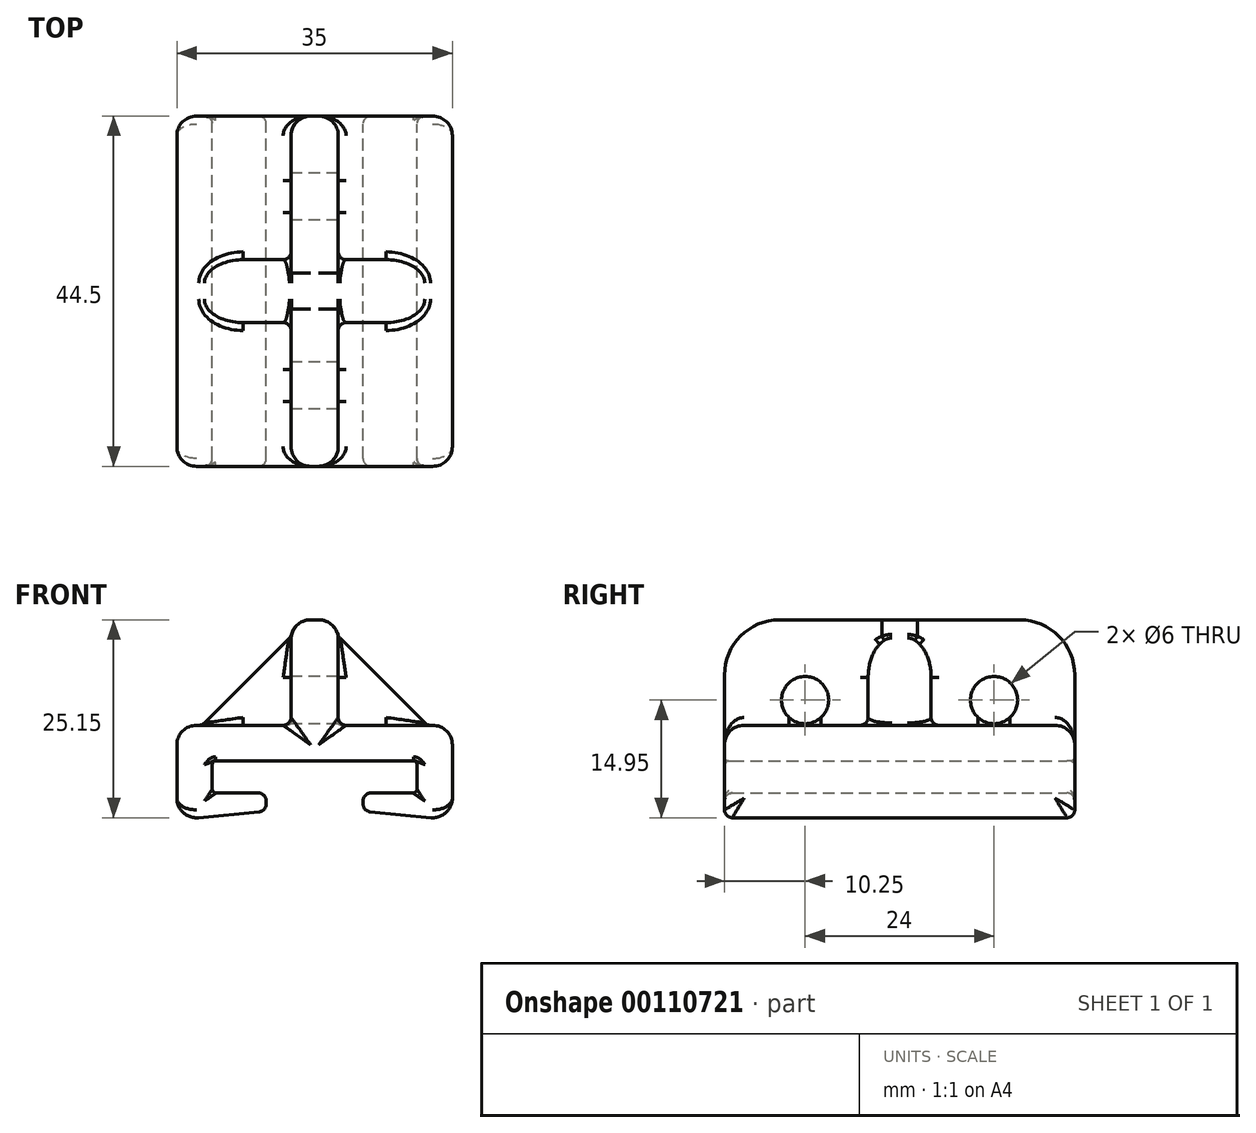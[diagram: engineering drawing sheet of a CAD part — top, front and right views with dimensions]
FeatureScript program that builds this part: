
annotation { "Feature Type Name" : "Feature", "Feature Type Description" : "" }
export const myFeature = defineFeature(function(context is Context, id is Id, definition is map)
    precondition{}
    {
        {
            var Q0;
            Q0=qCreatedBy(makeId("Front.planeOp"),FACE);
            var sketch = newSketch(context, id + "F0", { "sketchPlane" : qUnion([Q0])});
            skLineSegment(sketch, "E0", {"start": v(0, 0) * mm, "end": v(-13, 0) * mm});
            skLineSegment(sketch, "E1", {"start": v(-13, 0) * mm, "end": v(-13, -4.1) * mm});
            skLineSegment(sketch, "E2", {"start": v(-13, -4.1) * mm, "end": v(-6.15, -4.1) * mm});
            skLineSegment(sketch, "E3", {"start": v(-6.15, -4.1) * mm, "end": v(-6.15, -6.4) * mm});
            skLineSegment(sketch, "E4", {"start": v(-6.15, -6.4) * mm, "end": v(-17.5, -7.5) * mm});
            skLineSegment(sketch, "E5", {"start": v(-17.5, -7.5) * mm, "end": v(-17.5, 4.5) * mm});
            skLineSegment(sketch, "E6", {"start": v(-17.5, 4.5) * mm, "end": v(-3, 4.5) * mm});
            skLineSegment(sketch, "E7", {"start": v(-3, 4.5) * mm, "end": v(-3, 17.9) * mm});
            skLineSegment(sketch, "E8", {"start": v(-3, 17.9) * mm, "end": v(0, 17.9) * mm});
            skLineSegment(sketch, "E9.MirrorCS", {"start": v(6.15, -4.1) * mm, "end": v(6.15, -6.4) * mm});
            skLineSegment(sketch, "E10.MirrorCS", {"start": v(3, 17.9) * mm, "end": v(0, 17.9) * mm});
            skLineSegment(sketch, "E11.MirrorCS", {"start": v(13, -4.1) * mm, "end": v(6.15, -4.1) * mm});
            skLineSegment(sketch, "E12.MirrorCS", {"start": v(3, 4.5) * mm, "end": v(3, 17.9) * mm});
            skLineSegment(sketch, "E13.MirrorCS", {"start": v(17.5, 4.5) * mm, "end": v(3, 4.5) * mm});
            skLineSegment(sketch, "E14.MirrorCS", {"start": v(17.5, -7.5) * mm, "end": v(17.5, 4.5) * mm});
            skLineSegment(sketch, "E15.MirrorCS", {"start": v(6.15, -6.4) * mm, "end": v(17.5, -7.5) * mm});
            skLineSegment(sketch, "E16.MirrorCS", {"start": v(0, 0) * mm, "end": v(13, 0) * mm});
            skLineSegment(sketch, "E17.MirrorCS", {"start": v(13, 0) * mm, "end": v(13, -4.1) * mm});
            skSolve(sketch);
        }
        {
            var Q0;
            Q0=qSketchRegion(id+"F0",true);
            extrude(context, id + "F1", {"entities" : qUnion([Q0]), "depth" : 44.5 * mm, "symmetric" : true});
        }
        {
            var Q0;
            Q0=qCreatedBy(makeId("Front.planeOp"),FACE);
            var sketch = newSketch(context, id + "F2", { "sketchPlane" : qUnion([Q0])});
            skLineSegment(sketch, "E18.0", {"start": v(-3, 4.5) * mm, "end": v(-3, 15.8) * mm});
            skLineSegment(sketch, "E19.0", {"start": v(-14.3, 4.5) * mm, "end": v(-3, 4.5) * mm});
            skLineSegment(sketch, "E20", {"start": v(-14.3, 4.5) * mm, "end": v(-3, 15.8) * mm});
            skPoint(sketch, "E21.orphan", {"position": v(-3, 17.9) * mm});
            skPoint(sketch, "E22.orphan", {"position": v(-17.5, 4.5) * mm});
            skPoint(sketch, "E23.MirrorP", {"position": v(3, 17.9) * mm});
            skPoint(sketch, "E24.MirrorP", {"position": v(17.5, 4.5) * mm});
            skLineSegment(sketch, "E25.MirrorCS", {"start": v(3, 4.5) * mm, "end": v(3, 15.8) * mm});
            skLineSegment(sketch, "E26.MirrorCS", {"start": v(14.3, 4.5) * mm, "end": v(3, 15.8) * mm});
            skLineSegment(sketch, "E27.MirrorCS", {"start": v(14.3, 4.5) * mm, "end": v(3, 4.5) * mm});
            skSolve(sketch);
        }
        {
            var Q0;
            Q0=qSketchRegion(id+"F2",true);
            extrude(context, id + "F3", {"entities" : qUnion([Q0]), "operationType" : NewBodyOperationType.ADD, "depth" : 8 * mm, "symmetric" : true});
        }
        {
            var Q0;
            Q0=makeQuery(id+"F1.opExtrude","CAP_EDGE",EDGE,{"disambiguationData":[OSD([sQuery(id+"F0.wireOp",EDGE,"E8"),sQuery(id+"F0.wireOp",EDGE,"E10.MirrorCS")])],"isStart":false});
            var Q1;
            Q1=makeQuery(id+"F1.opExtrude","CAP_EDGE",EDGE,{"disambiguationData":[OSD([sQuery(id+"F0.wireOp",EDGE,"E8"),sQuery(id+"F0.wireOp",EDGE,"E10.MirrorCS")])],"isStart":true});
            fillet(context, id + "F4", {"entities" : qUnion([Q0, Q1]), "radius" : 7 * mm, "tangentPropagation" : true, "allowEdgeOverflow" : false});
        }
        {
            var Q0;
            Q0=makeQuery(id+"F1.opExtrude","SWEPT_FACE",FACE,{"disambiguationData":[OSD([sQuery(id+"F0.wireOp",EDGE,"E12.MirrorCS")])]});
            var sketch = newSketch(context, id + "F5", { "sketchPlane" : qUnion([Q0])});
            skPoint(sketch, "E28", {"position": v(-12, 7.7) * mm});
            skPoint(sketch, "E29", {"position": v(12, 7.7) * mm});
            skSolve(sketch);
        }
        {
            var Q0;
            Q0=sQuery(id+"F5.wireOp",VERTEX,"E28");
            var Q1;
            Q1=sQuery(id+"F5.wireOp",VERTEX,"E29");
            var Q2;
            Q2=makeQuery(id+"F1.opExtrude","SWEPT_BODY",BODY,{"disambiguationData":[OSD([sQuery(id+"F0.wireOp",EDGE,"E0"),sQuery(id+"F0.wireOp",EDGE,"E1"),sQuery(id+"F0.wireOp",EDGE,"E2"),sQuery(id+"F0.wireOp",EDGE,"E3"),sQuery(id+"F0.wireOp",EDGE,"E4"),sQuery(id+"F0.wireOp",EDGE,"E5"),sQuery(id+"F0.wireOp",EDGE,"E6"),sQuery(id+"F0.wireOp",EDGE,"E7"),sQuery(id+"F0.wireOp",EDGE,"E8"),sQuery(id+"F0.wireOp",EDGE,"E9.MirrorCS"),sQuery(id+"F0.wireOp",EDGE,"E10.MirrorCS"),sQuery(id+"F0.wireOp",EDGE,"E11.MirrorCS"),sQuery(id+"F0.wireOp",EDGE,"E12.MirrorCS"),sQuery(id+"F0.wireOp",EDGE,"E13.MirrorCS"),sQuery(id+"F0.wireOp",EDGE,"E14.MirrorCS"),sQuery(id+"F0.wireOp",EDGE,"E15.MirrorCS"),sQuery(id+"F0.wireOp",EDGE,"E16.MirrorCS"),sQuery(id+"F0.wireOp",EDGE,"E17.MirrorCS")])]});
            hole(context, id + "F6", {"style" : HoleStyle.SIMPLE, "endStyle" : HoleEndStyle.THROUGH, "holeDiameter" : 6 * mm, "locations" : qUnion([Q0, Q1]), "scope" : qUnion([Q2]), "isTappedThrough" : true, "startStyle" : HoleStartStyle.PART});
        }
        {
            var Q0;
            Q0=makeQuery(id+"F3.opExtrude","CAP_EDGE",EDGE,{"disambiguationData":[OSD([sQuery(id+"F2.wireOp",EDGE,"E26.MirrorCS")])],"isStart":false});
            var Q1;
            Q1=makeQuery(id+"F3.opExtrude","CAP_EDGE",EDGE,{"disambiguationData":[OSD([sQuery(id+"F2.wireOp",EDGE,"E26.MirrorCS")])],"isStart":true});
            var Q2;
            Q2=makeQuery(id+"F3.opExtrude","CAP_EDGE",EDGE,{"disambiguationData":[OSD([sQuery(id+"F2.wireOp",EDGE,"E20")])],"isStart":true});
            var Q3;
            Q3=makeQuery(id+"F3.opExtrude","CAP_EDGE",EDGE,{"disambiguationData":[OSD([sQuery(id+"F2.wireOp",EDGE,"E20")])],"isStart":false});
            fillet(context, id + "F7", {"entities" : qUnion([Q0, Q1, Q2, Q3]), "radius" : 3 * mm, "tangentPropagation" : true, "allowEdgeOverflow" : false});
        }
        {
            var Q0;
            Q0=makeQuery(id+"F1.opExtrude","SWEPT_EDGE",EDGE,{"disambiguationData":[OSD([sQuery(id+"F0.wireOp",EDGE,"E9.MirrorCS"),sQuery(id+"F0.wireOp",EDGE,"E15.MirrorCS")])]});
            var Q1;
            Q1=makeQuery(id+"F1.opExtrude","SWEPT_EDGE",EDGE,{"disambiguationData":[OSD([sQuery(id+"F0.wireOp",EDGE,"E9.MirrorCS"),sQuery(id+"F0.wireOp",EDGE,"E11.MirrorCS")])]});
            var Q2;
            Q2=makeQuery(id+"F1.opExtrude","SWEPT_EDGE",EDGE,{"disambiguationData":[OSD([sQuery(id+"F0.wireOp",EDGE,"E2"),sQuery(id+"F0.wireOp",EDGE,"E3")])]});
            var Q3;
            Q3=makeQuery(id+"F1.opExtrude","SWEPT_EDGE",EDGE,{"disambiguationData":[OSD([sQuery(id+"F0.wireOp",EDGE,"E3"),sQuery(id+"F0.wireOp",EDGE,"E4")])]});
            fillet(context, id + "F8", {"entities" : qUnion([Q0, Q1, Q2, Q3]), "radius" : 1 * mm, "tangentPropagation" : true, "allowEdgeOverflow" : false});
        }
        {
            var Q0;
            Q0=makeQuery(id+"F1.opExtrude","SWEPT_FACE",FACE,{"disambiguationData":[OSD([sQuery(id+"F0.wireOp",EDGE,"E14.MirrorCS")])]});
            var Q1;
            Q1=makeQuery(id+"F1.opExtrude","SWEPT_FACE",FACE,{"disambiguationData":[OSD([sQuery(id+"F0.wireOp",EDGE,"E5")])]});
            var Q2;
            Q2=makeQuery(id+"F1.opExtrude","SWEPT_EDGE",EDGE,{"disambiguationData":[OSD([sQuery(id+"F0.wireOp",EDGE,"E7"),sQuery(id+"F0.wireOp",EDGE,"E8")])]});
            var Q3;
            Q3=makeQuery(id+"F1.opExtrude","SWEPT_EDGE",EDGE,{"disambiguationData":[OSD([sQuery(id+"F0.wireOp",EDGE,"E10.MirrorCS"),sQuery(id+"F0.wireOp",EDGE,"E12.MirrorCS")])]});
            var Q4;
            Q4=makeQuery(id+"F1.opExtrude","CAP_EDGE",EDGE,{"disambiguationData":[OSD([sQuery(id+"F0.wireOp",EDGE,"E13.MirrorCS")])],"isStart":true});
            var Q5;
            Q5=makeQuery(id+"F1.opExtrude","CAP_EDGE",EDGE,{"disambiguationData":[OSD([sQuery(id+"F0.wireOp",EDGE,"E6")])],"isStart":true});
            var Q6;
            Q6=makeQuery(id+"F1.opExtrude","CAP_EDGE",EDGE,{"disambiguationData":[OSD([sQuery(id+"F0.wireOp",EDGE,"E13.MirrorCS")])],"isStart":false});
            var Q7;
            Q7=makeQuery(id+"F1.opExtrude","CAP_EDGE",EDGE,{"disambiguationData":[OSD([sQuery(id+"F0.wireOp",EDGE,"E6")])],"isStart":false});
            fillet(context, id + "F9", {"entities" : qUnion([Q0, Q1, Q2, Q3, Q4, Q5, Q6, Q7]), "radius" : 2.5 * mm, "tangentPropagation" : true, "allowEdgeOverflow" : false});
        }
        {
            var Q0;
            Q0=makeQuery(id+"F3.opExtrude","CAP_EDGE",EDGE,{"disambiguationData":[OSD([sQuery(id+"F2.wireOp",EDGE,"E19.0")])],"isStart":true});
            var Q1;
            Q1=makeQuery(id+"F3.opExtrude","CAP_EDGE",EDGE,{"disambiguationData":[OSD([sQuery(id+"F2.wireOp",EDGE,"E18.0")])],"isStart":true});
            var Q2;
            Q2=makeQuery(id+"F3.opExtrude","CAP_FACE",FACE,{"disambiguationData":[OSD([sQuery(id+"F2.wireOp",EDGE,"E25.MirrorCS"),sQuery(id+"F2.wireOp",EDGE,"E26.MirrorCS"),sQuery(id+"F2.wireOp",EDGE,"E27.MirrorCS")])],"isStart":true});
            var Q3;
            Q3=makeQuery(id+"F3.opExtrude","CAP_FACE",FACE,{"disambiguationData":[OSD([sQuery(id+"F2.wireOp",EDGE,"E25.MirrorCS"),sQuery(id+"F2.wireOp",EDGE,"E26.MirrorCS"),sQuery(id+"F2.wireOp",EDGE,"E27.MirrorCS")])],"isStart":false});
            var Q4;
            Q4=makeQuery(id+"F3.opExtrude","CAP_FACE",FACE,{"disambiguationData":[OSD([sQuery(id+"F2.wireOp",EDGE,"E18.0"),sQuery(id+"F2.wireOp",EDGE,"E19.0"),sQuery(id+"F2.wireOp",EDGE,"E20")])],"isStart":false});
            var Q5;
            Q5=makeQuery(id+"F1.opExtrude","CAP_EDGE",EDGE,{"disambiguationData":[OSD([sQuery(id+"F0.wireOp",EDGE,"E4")])],"isStart":false});
            var Q6;
            Q6=makeQuery(id+"F1.opExtrude","CAP_EDGE",EDGE,{"disambiguationData":[OSD([sQuery(id+"F0.wireOp",EDGE,"E15.MirrorCS")])],"isStart":false});
            var Q7;
            Q7=makeQuery(id+"F1.opExtrude","CAP_EDGE",EDGE,{"disambiguationData":[OSD([sQuery(id+"F0.wireOp",EDGE,"E17.MirrorCS")])],"isStart":false});
            var Q8;
            Q8=makeQuery(id+"F1.opExtrude","CAP_EDGE",EDGE,{"disambiguationData":[OSD([sQuery(id+"F0.wireOp",EDGE,"E1")])],"isStart":false});
            var Q9;
            Q9=makeQuery(id+"F1.opExtrude","CAP_EDGE",EDGE,{"disambiguationData":[OSD([sQuery(id+"F0.wireOp",EDGE,"E2")])],"isStart":true});
            var Q10;
            Q10=makeQuery(id+"F1.opExtrude","CAP_EDGE",EDGE,{"disambiguationData":[OSD([sQuery(id+"F0.wireOp",EDGE,"E1")])],"isStart":true});
            var Q11;
            Q11=makeQuery(id+"F1.opExtrude","CAP_EDGE",EDGE,{"disambiguationData":[OSD([sQuery(id+"F0.wireOp",EDGE,"E11.MirrorCS")])],"isStart":true});
            var Q12;
            Q12=makeQuery(id+"F1.opExtrude","CAP_EDGE",EDGE,{"disambiguationData":[OSD([sQuery(id+"F0.wireOp",EDGE,"E17.MirrorCS")])],"isStart":true});
            fillet(context, id + "F10", {"entities" : qUnion([Q0, Q1, Q2, Q3, Q4, Q5, Q6, Q7, Q8, Q9, Q10, Q11, Q12]), "radius" : 1 * mm, "tangentPropagation" : true, "allowEdgeOverflow" : false});
        }
        {
            var Q0;
            Q0=makeQuery(id+"F1.opExtrude","SWEPT_EDGE",EDGE,{"disambiguationData":[OSD([sQuery(id+"F0.wireOp",EDGE,"E11.MirrorCS"),sQuery(id+"F0.wireOp",EDGE,"E17.MirrorCS")])]});
            var Q1;
            Q1=makeQuery(id+"F1.opExtrude","SWEPT_EDGE",EDGE,{"disambiguationData":[OSD([sQuery(id+"F0.wireOp",EDGE,"E1"),sQuery(id+"F0.wireOp",EDGE,"E2")])]});
            var Q2;
            Q2=makeQuery(id+"F1.opExtrude","SWEPT_FACE",FACE,{"disambiguationData":[OSD([sQuery(id+"F0.wireOp",EDGE,"E0"),sQuery(id+"F0.wireOp",EDGE,"E16.MirrorCS")])]});
            var Q3;
            Q3=makeQuery(id+"F6.hole-1.boolean.opBoolean","COPY",FACE,{"derivedFrom":makeQuery(id+"F6.hole-1.opRevolve","SWEPT_FACE",FACE,{"disambiguationData":[OSD([sQuery(id+"F6.hole-1.sketch.wireOp",EDGE,"core_line_2")])]})});
            var Q4;
            Q4=makeQuery(id+"F6.hole-0.boolean.opBoolean","COPY",FACE,{"derivedFrom":makeQuery(id+"F6.hole-0.opRevolve","SWEPT_FACE",FACE,{"disambiguationData":[OSD([sQuery(id+"F6.hole-0.sketch.wireOp",EDGE,"core_line_2")])]})});
            fillet(context, id + "F11", {"entities" : qUnion([Q0, Q1, Q2, Q3, Q4]), "radius" : .5 * mm, "tangentPropagation" : true, "allowEdgeOverflow" : false});
        }
        {
            var Q0;
            {var subQ0=sQuery(id+"F0.wireOp",EDGE,"E7");var subQ1=sQuery(id+"F0.wireOp",EDGE,"E6");Q0=makeQuery(id+"F3.boolean.opBoolean","SPLIT",EDGE,{"disambiguationData":[TD([makeQuery(id+"F3.opExtrude","CAP_FACE",FACE,{"disambiguationData":[OSD([sQuery(id+"F2.wireOp",EDGE,"E18.0"),sQuery(id+"F2.wireOp",EDGE,"E19.0"),sQuery(id+"F2.wireOp",EDGE,"E20")])],"isStart":true})])],"derivedFrom":makeQuery(id+"F1.opExtrude","SWEPT_EDGE",EDGE,{"disambiguationData":[OSD([subQ1,subQ0])]})});}
            var Q1;
            {var subQ0=sQuery(id+"F0.wireOp",EDGE,"E7");var subQ1=sQuery(id+"F0.wireOp",EDGE,"E6");Q1=makeQuery(id+"F3.boolean.opBoolean","SPLIT",EDGE,{"disambiguationData":[TD([makeQuery(id+"F3.opExtrude","CAP_FACE",FACE,{"disambiguationData":[OSD([sQuery(id+"F2.wireOp",EDGE,"E18.0"),sQuery(id+"F2.wireOp",EDGE,"E19.0"),sQuery(id+"F2.wireOp",EDGE,"E20")])],"isStart":true})])],"derivedFrom":makeQuery(id+"F1.opExtrude","SWEPT_EDGE",EDGE,{"disambiguationData":[OSD([subQ1,subQ0])]})});}
            var Q2;
            {var subQ0=sQuery(id+"F0.wireOp",EDGE,"E7");var subQ1=sQuery(id+"F0.wireOp",EDGE,"E6");Q2=makeQuery(id+"F3.boolean.opBoolean","SPLIT",EDGE,{"disambiguationData":[TD([makeQuery(id+"F3.opExtrude","CAP_FACE",FACE,{"disambiguationData":[OSD([sQuery(id+"F2.wireOp",EDGE,"E18.0"),sQuery(id+"F2.wireOp",EDGE,"E19.0"),sQuery(id+"F2.wireOp",EDGE,"E20")])],"isStart":false})])],"derivedFrom":makeQuery(id+"F1.opExtrude","SWEPT_EDGE",EDGE,{"disambiguationData":[OSD([subQ1,subQ0])]})});}
            var Q3;
            {var subQ0=sQuery(id+"F0.wireOp",EDGE,"E7");var subQ1=sQuery(id+"F0.wireOp",EDGE,"E6");Q3=makeQuery(id+"F3.boolean.opBoolean","SPLIT",EDGE,{"disambiguationData":[TD([makeQuery(id+"F3.opExtrude","CAP_FACE",FACE,{"disambiguationData":[OSD([sQuery(id+"F2.wireOp",EDGE,"E18.0"),sQuery(id+"F2.wireOp",EDGE,"E19.0"),sQuery(id+"F2.wireOp",EDGE,"E20")])],"isStart":false})])],"derivedFrom":makeQuery(id+"F1.opExtrude","SWEPT_EDGE",EDGE,{"disambiguationData":[OSD([subQ1,subQ0])]})});}
            var Q4;
            {var subQ0=sQuery(id+"F0.wireOp",EDGE,"E13.MirrorCS");var subQ1=sQuery(id+"F0.wireOp",EDGE,"E12.MirrorCS");Q4=makeQuery(id+"F3.boolean.opBoolean","SPLIT",EDGE,{"disambiguationData":[TD([makeQuery(id+"F3.opExtrude","CAP_FACE",FACE,{"disambiguationData":[OSD([sQuery(id+"F2.wireOp",EDGE,"E25.MirrorCS"),sQuery(id+"F2.wireOp",EDGE,"E26.MirrorCS"),sQuery(id+"F2.wireOp",EDGE,"E27.MirrorCS")])],"isStart":true})])],"derivedFrom":makeQuery(id+"F1.opExtrude","SWEPT_EDGE",EDGE,{"disambiguationData":[OSD([subQ1,subQ0])]})});}
            var Q5;
            {var subQ0=sQuery(id+"F0.wireOp",EDGE,"E13.MirrorCS");var subQ1=sQuery(id+"F0.wireOp",EDGE,"E12.MirrorCS");Q5=makeQuery(id+"F3.boolean.opBoolean","SPLIT",EDGE,{"disambiguationData":[TD([makeQuery(id+"F3.opExtrude","CAP_FACE",FACE,{"disambiguationData":[OSD([sQuery(id+"F2.wireOp",EDGE,"E25.MirrorCS"),sQuery(id+"F2.wireOp",EDGE,"E26.MirrorCS"),sQuery(id+"F2.wireOp",EDGE,"E27.MirrorCS")])],"isStart":true})])],"derivedFrom":makeQuery(id+"F1.opExtrude","SWEPT_EDGE",EDGE,{"disambiguationData":[OSD([subQ1,subQ0])]})});}
            var Q6;
            {var subQ0=sQuery(id+"F0.wireOp",EDGE,"E13.MirrorCS");var subQ1=sQuery(id+"F0.wireOp",EDGE,"E12.MirrorCS");Q6=makeQuery(id+"F3.boolean.opBoolean","SPLIT",EDGE,{"disambiguationData":[TD([makeQuery(id+"F3.opExtrude","CAP_FACE",FACE,{"disambiguationData":[OSD([sQuery(id+"F2.wireOp",EDGE,"E25.MirrorCS"),sQuery(id+"F2.wireOp",EDGE,"E26.MirrorCS"),sQuery(id+"F2.wireOp",EDGE,"E27.MirrorCS")])],"isStart":false})])],"derivedFrom":makeQuery(id+"F1.opExtrude","SWEPT_EDGE",EDGE,{"disambiguationData":[OSD([subQ1,subQ0])]})});}
            fillet(context, id + "F12", {"entities" : qUnion([Q0, Q1, Q2, Q3, Q4, Q5, Q6]), "radius" : 1 * mm, "tangentPropagation" : true, "allowEdgeOverflow" : false});
        }
    });
